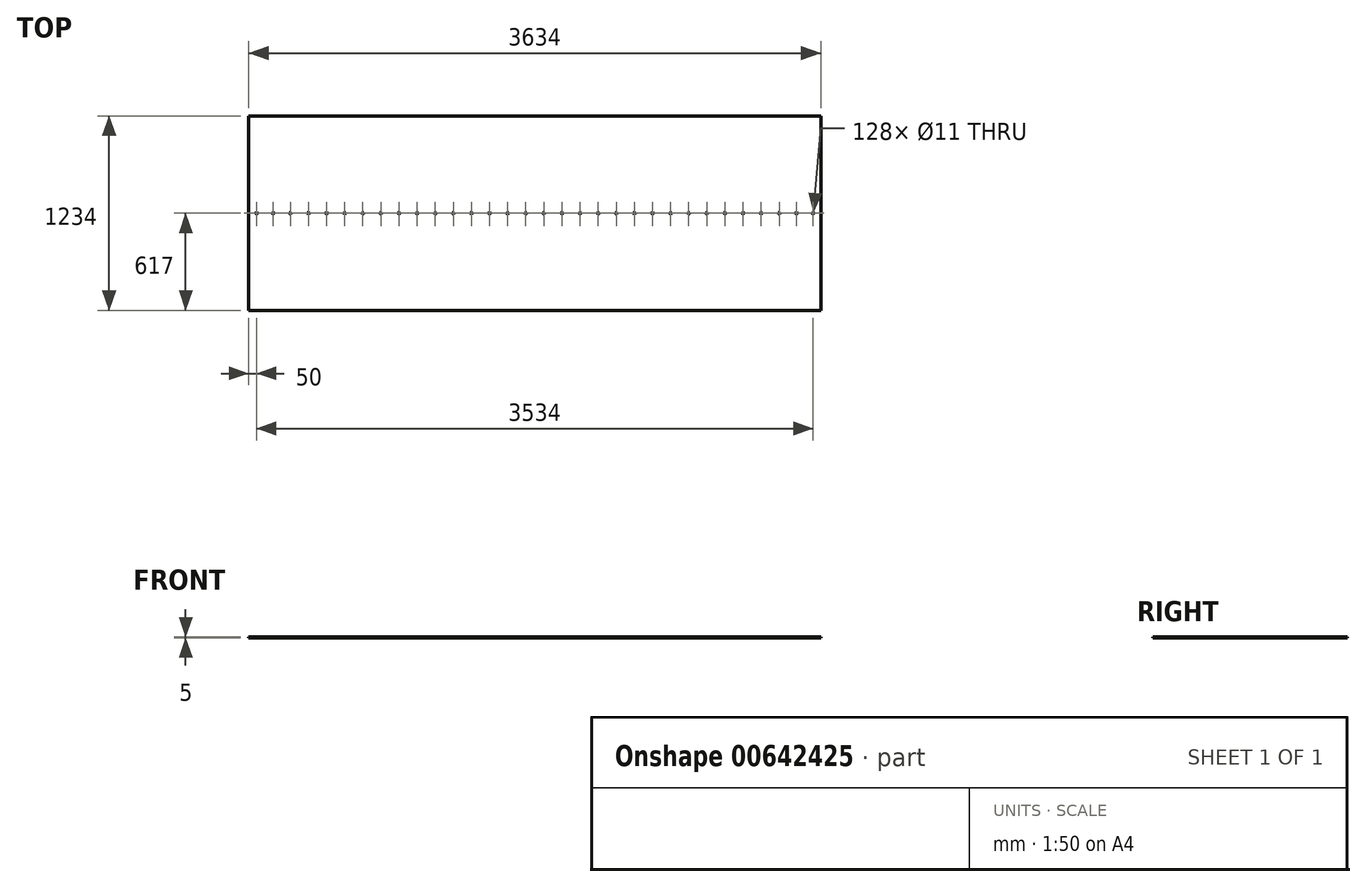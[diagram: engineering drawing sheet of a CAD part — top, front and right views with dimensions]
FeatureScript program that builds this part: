
annotation { "Feature Type Name" : "Feature", "Feature Type Description" : "" }
export const myFeature = defineFeature(function(context is Context, id is Id, definition is map)
    precondition{}
    {
        {
            var Q0;
            Q0=qCreatedBy(makeId("Top.planeOp"),FACE);
            var sketch = newSketch(context, id + "F0", { "sketchPlane" : qUnion([Q0])});
            skLineSegment(sketch, "E0.bottom", {"start": v(1817, -617) * mm, "end": v(-1817, -617) * mm});
            skLineSegment(sketch, "E0.top", {"start": v(1817, 617) * mm, "end": v(-1817, 617) * mm});
            skLineSegment(sketch, "E0.left", {"start": v(1817, -617) * mm, "end": v(1817, 617) * mm});
            skLineSegment(sketch, "E0.right", {"start": v(-1817, -617) * mm, "end": v(-1817, 617) * mm});
            skPoint(sketch, "E0.middle", {"position": v(0, 0) * mm});
            skSolve(sketch);
        }
        {
            var Q0;
            Q0=makeQuery(id+"F0.imprint","IMPRINT",FACE,{"disambiguationData":[TD([[makeQuery(id+"F0.imprint","IMPRINT",EDGE,{"derivedFrom":sQuery(id+"F0.wireOp",EDGE,"E0.bottom")}),-1.0]])]});
            extrude(context, id + "F1", {"entities" : qUnion([Q0]), "depth" : 5 * mm, "offsetDistance" : 25 * mm});
        }
        {
            var Q0;
            Q0=makeQuery(id+"F1.opExtrude","CAP_FACE",FACE,{"disambiguationData":[OSD([sQuery(id+"F0.wireOp",EDGE,"E0.bottom"),sQuery(id+"F0.wireOp",EDGE,"E0.top"),sQuery(id+"F0.wireOp",EDGE,"E0.left"),sQuery(id+"F0.wireOp",EDGE,"E0.right")])],"isStart":false});
            var sketch = newSketch(context, id + "F2", { "sketchPlane" : qUnion([Q0])});
            skLineSegment(sketch, "E1", {"start": v(0, -617) * mm, "end": v(0, 617) * mm, "construction": true});
            skCircle(sketch, "E2", {"center": v(57.5, 0) * mm, "radius": 5.5 * mm});
            skCircle(sketch, "E3.1.0.0", {"center": v(172.5, 0) * mm, "radius": 5.5 * mm});
            skCircle(sketch, "E3.2.0.0", {"center": v(287.5, 0) * mm, "radius": 5.5 * mm});
            skCircle(sketch, "E3.3.0.0", {"center": v(402.5, 0) * mm, "radius": 5.5 * mm});
            skCircle(sketch, "E3.4.0.0", {"center": v(517.5, 0) * mm, "radius": 5.5 * mm});
            skCircle(sketch, "E3.5.0.0", {"center": v(632.5, 0) * mm, "radius": 5.5 * mm});
            skCircle(sketch, "E3.6.0.0", {"center": v(747.5, 0) * mm, "radius": 5.5 * mm});
            skCircle(sketch, "E3.7.0.0", {"center": v(862.5, 0) * mm, "radius": 5.5 * mm});
            skCircle(sketch, "E3.8.0.0", {"center": v(977.5, 0) * mm, "radius": 5.5 * mm});
            skCircle(sketch, "E3.9.0.0", {"center": v(1092.5, 0) * mm, "radius": 5.5 * mm});
            skCircle(sketch, "E3.10.0.0", {"center": v(1207.5, 0) * mm, "radius": 5.5 * mm});
            skCircle(sketch, "E3.11.0.0", {"center": v(1322.5, 0) * mm, "radius": 5.5 * mm});
            skCircle(sketch, "E3.12.0.0", {"center": v(1437.5, 0) * mm, "radius": 5.5 * mm});
            skCircle(sketch, "E3.13.0.0", {"center": v(1552.5, 0) * mm, "radius": 5.5 * mm});
            skLineSegment(sketch, "E3.direction1", {"start": v(57.5, 0) * mm, "end": v(172.5, 0) * mm, "construction": true});
            skCircle(sketch, "E4", {"center": v(-57.5, 0) * mm, "radius": 5.5 * mm});
            skCircle(sketch, "E5.1.0.0", {"center": v(-172.5, 0) * mm, "radius": 5.5 * mm});
            skCircle(sketch, "E5.2.0.0", {"center": v(-287.5, 0) * mm, "radius": 5.5 * mm});
            skLineSegment(sketch, "E5.direction1", {"start": v(-57.5, 0) * mm, "end": v(-172.5, 0) * mm, "construction": true});
            skLineSegment(sketch, "E5.direction2", {"start": v(-57.5, 0) * mm, "end": v(-57.5, 25) * mm, "construction": true});
            skCircle(sketch, "E6.0.3.0", {"center": v(-402.5, 0) * mm, "radius": 5.5 * mm});
            skCircle(sketch, "E6.0.4.0", {"center": v(-517.5, 0) * mm, "radius": 5.5 * mm});
            skCircle(sketch, "E6.0.5.0", {"center": v(-632.5, 0) * mm, "radius": 5.5 * mm});
            skCircle(sketch, "E6.0.6.0", {"center": v(-747.5, 0) * mm, "radius": 5.5 * mm});
            skCircle(sketch, "E6.0.7.0", {"center": v(-862.5, 0) * mm, "radius": 5.5 * mm});
            skCircle(sketch, "E6.0.8.0", {"center": v(-977.5, 0) * mm, "radius": 5.5 * mm});
            skCircle(sketch, "E6.0.9.0", {"center": v(-1092.5, 0) * mm, "radius": 5.5 * mm});
            skCircle(sketch, "E6.0.10.0", {"center": v(-1207.5, 0) * mm, "radius": 5.5 * mm});
            skCircle(sketch, "E6.0.11.0", {"center": v(-1322.5, 0) * mm, "radius": 5.5 * mm});
            skCircle(sketch, "E6.0.12.0", {"center": v(-1437.5, 0) * mm, "radius": 5.5 * mm});
            skCircle(sketch, "E6.0.13.0", {"center": v(-1552.5, 0) * mm, "radius": 5.5 * mm});
            skLineSegment(sketch, "E7.0", {"start": v(1817, -617) * mm, "end": v(1817, 617) * mm});
            skCircle(sketch, "E8", {"center": v(1767, 0) * mm, "radius": 5.5 * mm});
            skPoint(sketch, "E8.centerSnap0", {"position": v(1817, 0) * mm});
            skCircle(sketch, "E9", {"center": v(1662, 0) * mm, "radius": 5.5 * mm});
            skCircle(sketch, "E10", {"center": v(-1767, 0) * mm, "radius": 5.5 * mm});
            skPoint(sketch, "E10.centerSnap0", {"position": v(-1817, 0) * mm});
            skCircle(sketch, "E11", {"center": v(-1662, 0) * mm, "radius": 5.5 * mm});
            skSolve(sketch);
        }
        {
            var Q0;
            Q0=makeQuery(id+"F2.imprint","IMPRINT",FACE,{"disambiguationData":[TD([[makeQuery(id+"F2.imprint","IMPRINT",EDGE,{"derivedFrom":sQuery(id+"F2.wireOp",EDGE,"E2")}),1.0]])]});
            extrude(context, id + "F3", {"entities" : qUnion([Q0]), "operationType" : NewBodyOperationType.REMOVE, "endBound" : BoundingType.UP_TO_NEXT, "oppositeDirection" : true, "depth" : 25 * mm, "offsetDistance" : 25 * mm});
        }
        {
            var Q0;
            Q0 = qSketchRegion(id + "F2", true);
            var Q1;
            Q1=makeQuery(id+"F1.opExtrude","CAP_FACE",FACE,{"disambiguationData":[OSD([sQuery(id+"F0.wireOp",EDGE,"E0.bottom"),sQuery(id+"F0.wireOp",EDGE,"E0.top"),sQuery(id+"F0.wireOp",EDGE,"E0.left"),sQuery(id+"F0.wireOp",EDGE,"E0.right")])],"isStart":true});
            extrude(context, id + "F4", {"entities" : qUnion([Q0]), "operationType" : NewBodyOperationType.REMOVE, "endBound" : BoundingType.UP_TO_SURFACE, "oppositeDirection" : true, "depth" : 25 * mm, "endBoundEntityFace" : qUnion([Q1]), "offsetDistance" : 25 * mm});
        }
    });
